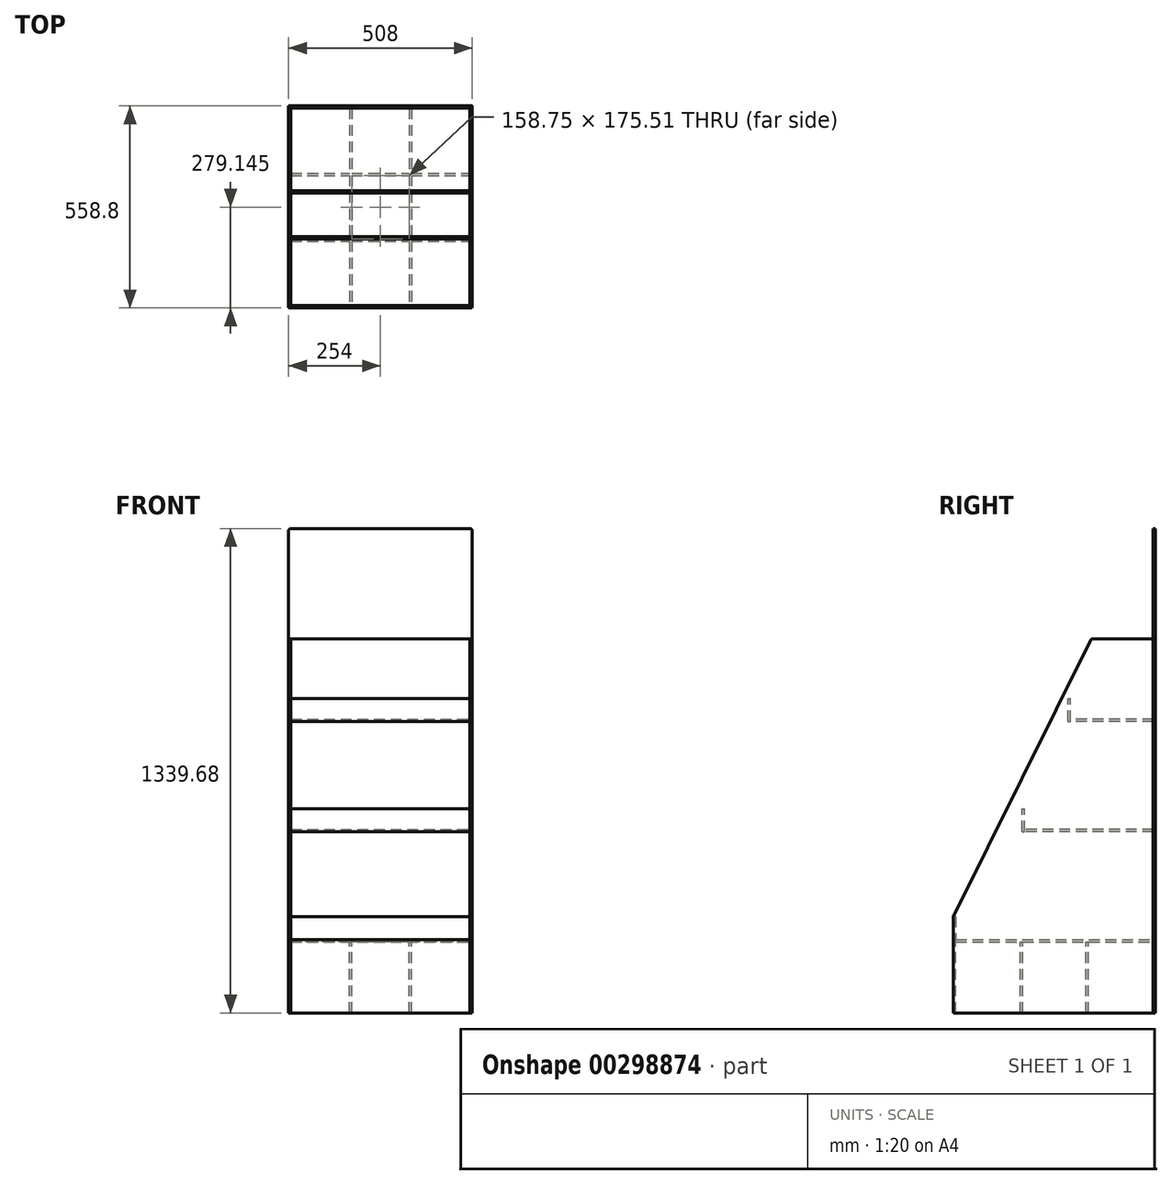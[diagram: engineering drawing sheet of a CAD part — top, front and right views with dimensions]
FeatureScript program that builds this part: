
annotation { "Feature Type Name" : "Feature", "Feature Type Description" : "" }
export const myFeature = defineFeature(function(context is Context, id is Id, definition is map)
    precondition{}
    {
        {
            var Q0;
            Q0=qCreatedBy(makeId("Right.planeOp"),FACE);
            var sketch = newSketch(context, id + "F0", { "sketchPlane" : qUnion([Q0])});
            skLineSegment(sketch, "E0", {"start": v(-313.65, -79.95) * mm, "end": v(245.15, -79.95) * mm});
            skLineSegment(sketch, "E1", {"start": v(245.15, 954.93) * mm, "end": v(67.35, 954.93) * mm});
            skLineSegment(sketch, "E2", {"start": v(-313.65, -79.95) * mm, "end": v(-313.65, 123.25) * mm});
            skLineSegment(sketch, "E3", {"start": v(-313.65, 123.25) * mm, "end": v(-313.65, 428.05) * mm, "construction": true});
            skLineSegment(sketch, "E4", {"start": v(-313.65, 428.05) * mm, "end": v(2.06, 428.05) * mm, "construction": true});
            skLineSegment(sketch, "E5", {"start": v(2.06, 428.05) * mm, "end": v(2.06, 732.85) * mm, "construction": true});
            skLineSegment(sketch, "E6", {"start": v(245.15, -79.95) * mm, "end": v(245.15, 954.93) * mm});
            skLineSegment(sketch, "E7", {"start": v(2.06, 732.85) * mm, "end": v(245.15, 732.85) * mm, "construction": true});
            skLineSegment(sketch, "E8", {"start": v(16.55, 732.85) * mm, "end": v(16.55, 796.35) * mm, "construction": true});
            skLineSegment(sketch, "E9", {"start": v(16.55, 796.35) * mm, "end": v(245.15, 796.35) * mm, "construction": true});
            skLineSegment(sketch, "E10", {"start": v(-313.65, 123.25) * mm, "end": v(-313.65, 186.75) * mm});
            skLineSegment(sketch, "E11", {"start": v(-313.65, 186.75) * mm, "end": v(67.35, 954.93) * mm});
            skSolve(sketch);
        }
        {
            var Q0;
            Q0 = qSketchRegion(id + "F0", true);
            extrude(context, id + "F1", {"entities" : qUnion([Q0]), "depth" : 6.35 * mm});
        }
        {
            var Q0;
            Q0=makeQuery(id+"F1.opExtrude","SWEPT_FACE",FACE,{"disambiguationData":[OSD([sQuery(id+"F0.wireOp",EDGE,"E6")])]});
            var sketch = newSketch(context, id + "F2", { "sketchPlane" : qUnion([Q0])});
            skLineSegment(sketch, "E12.bottom", {"start": v(-6.35, 954.93) * mm, "end": v(501.65, 954.93) * mm});
            skLineSegment(sketch, "E12.top", {"start": v(-6.35, -79.95) * mm, "end": v(501.65, -79.95) * mm});
            skLineSegment(sketch, "E12.left", {"start": v(-6.35, 954.93) * mm, "end": v(-6.35, -79.95) * mm});
            skLineSegment(sketch, "E12.right", {"start": v(501.65, 954.93) * mm, "end": v(501.65, -79.95) * mm});
            skSolve(sketch);
        }
        {
            var Q0;
            Q0 = qSketchRegion(id + "F2", true);
            extrude(context, id + "F3", {"entities" : qUnion([Q0]), "oppositeDirection" : true, "depth" : 6.35 * mm});
        }
        {
            var Q0;
            Q0=makeQuery(id+"F3.opExtrude","CAP_EDGE",EDGE,{"disambiguationData":[OSD([sQuery(id+"F2.wireOp",EDGE,"E12.bottom")])],"isStart":true});
            cPoint(context, id + "F4", {"entities" : qUnion([Q0]), "parameter" : 0.5});
        }
        {
            var Q0;
            Q0=qCreatedBy(makeId("Right.planeOp"),FACE);
            var Q1;
            Q1 = qCreatedBy(id + "F4" ,VERTEX);
            cPlane(context, id + "F5", {"entities" : qUnion([Q0, Q1]), "cplaneType" : CPlaneType.PLANE_POINT, "offset" : 25.4 * mm, "width" : 152.4 * mm, "height" : 152.4 * mm});
        }
        {
            var Q0;
            Q0=makeQuery(id+"F1.opExtrude","SWEPT_BODY",BODY,{"disambiguationData":[OSD([sQuery(id+"F0.wireOp",EDGE,"E0"),sQuery(id+"F0.wireOp",EDGE,"E1"),sQuery(id+"F0.wireOp",EDGE,"E2"),sQuery(id+"F0.wireOp",EDGE,"AbcFDwva-9bQH-yg0s-ynAT-r469iKRznc1V"),sQuery(id+"F0.wireOp",EDGE,"E6")])]});
            var Q1;
            Q1=qCreatedBy(id+"F5.planeOp",FACE);
            mirror(context, id + "F6", {"entities" : qUnion([Q0]), "mirrorPlane" : qUnion([Q1])});
        }
        {
            var Q0;
            Q0=makeQuery(id+"F6.opPattern","COPY",FACE,{"derivedFrom":makeQuery(id+"F1.opExtrude","SWEPT_FACE",FACE,{"disambiguationData":[OSD([sQuery(id+"F0.wireOp",EDGE,"E2")])]}),"instanceName":"1"});
            var sketch = newSketch(context, id + "F7", { "sketchPlane" : qUnion([Q0])});
            skLineSegment(sketch, "E13.bottom", {"start": v(-495.3, -79.95) * mm, "end": v(0, -79.95) * mm});
            skLineSegment(sketch, "E13.top", {"start": v(-495.3, 123.33) * mm, "end": v(0, 123.33) * mm});
            skLineSegment(sketch, "E13.left", {"start": v(-495.3, -79.95) * mm, "end": v(-495.3, 123.33) * mm});
            skLineSegment(sketch, "E13.right", {"start": v(0, -79.95) * mm, "end": v(0, 123.33) * mm});
            skSolve(sketch);
        }
        {
            var Q0;
            Q0 = qSketchRegion(id + "F7", true);
            extrude(context, id + "F8", {"entities" : qUnion([Q0]), "oppositeDirection" : true, "depth" : 6.35 * mm});
        }
        {
            var Q0;
            Q0=makeQuery(id+"F8.opExtrude","SWEPT_FACE",FACE,{"disambiguationData":[OSD([sQuery(id+"F7.wireOp",EDGE,"E13.top")])]});
            var sketch = newSketch(context, id + "F9", { "sketchPlane" : qUnion([Q0])});
            skLineSegment(sketch, "E14.bottom", {"start": v(-495.3, -313.65) * mm, "end": v(0, -313.65) * mm});
            skLineSegment(sketch, "E14.top", {"start": v(-495.3, 238.8) * mm, "end": v(0, 238.8) * mm});
            skLineSegment(sketch, "E14.left", {"start": v(-495.3, -313.65) * mm, "end": v(-495.3, 238.8) * mm});
            skLineSegment(sketch, "E14.right", {"start": v(0, -313.65) * mm, "end": v(0, 238.8) * mm});
            skSolve(sketch);
        }
        {
            var Q0;
            {var subQ0=sQuery(id+"F9.wireOp",EDGE,"E14.top");Q0=makeQuery(id+"F9.imprint","IMPRINT",FACE,{"disambiguationData":[TD([[makeQuery(id+"F9.imprint","IMPRINT",EDGE,{"derivedFrom":subQ0}),-1.0]])]});}
            extrude(context, id + "F10", {"entities" : qUnion([Q0]), "oppositeDirection" : true, "depth" : 6.35 * mm});
        }
        {
            var Q0;
            Q0=qCreatedBy(makeId("Top.planeOp"),FACE);
            var Q1;
            Q1=sQuery(id+"F0.wireOp",VERTEX,"E5.start");
            cPlane(context, id + "F11", {"entities" : qUnion([Q0, Q1]), "cplaneType" : CPlaneType.PLANE_POINT, "offset" : 25.4 * mm, "width" : 152.4 * mm, "height" : 152.4 * mm});
        }
        {
            var Q0;
            Q0=qCreatedBy(id+"F11.planeOp",FACE);
            var sketch = newSketch(context, id + "F12", { "sketchPlane" : qUnion([Q0])});
            skLineSegment(sketch, "E15.0", {"start": v(6.35, 238.8) * mm, "end": v(-501.65, 238.8) * mm, "construction": true});
            skLineSegment(sketch, "E16.bottom", {"start": v(-495.3, 238.8) * mm, "end": v(0, 238.8) * mm});
            skLineSegment(sketch, "E16.top", {"start": v(-495.3, -116.8) * mm, "end": v(0, -116.8) * mm});
            skLineSegment(sketch, "E16.left", {"start": v(-495.3, 238.8) * mm, "end": v(-495.3, -116.8) * mm});
            skLineSegment(sketch, "E16.right", {"start": v(0, 238.8) * mm, "end": v(0, -116.8) * mm});
            skSolve(sketch);
        }
        {
            var Q0;
            Q0 = qSketchRegion(id + "F12", true);
            extrude(context, id + "F13", {"entities" : qUnion([Q0]), "oppositeDirection" : true, "depth" : 6.35 * mm});
        }
        {
            var Q0;
            Q0=makeQuery(id+"F13.opExtrude","SWEPT_FACE",FACE,{"disambiguationData":[OSD([sQuery(id+"F12.wireOp",EDGE,"E16.top")])]});
            var sketch = newSketch(context, id + "F14", { "sketchPlane" : qUnion([Q0])});
            skLineSegment(sketch, "E17.0", {"start": v(-495.3, 421.7) * mm, "end": v(0, 421.7) * mm, "construction": true});
            skLineSegment(sketch, "E18.bottom", {"start": v(-495.3, 421.7) * mm, "end": v(0, 421.7) * mm});
            skLineSegment(sketch, "E18.top", {"start": v(-495.3, 485.2) * mm, "end": v(0, 485.2) * mm});
            skLineSegment(sketch, "E18.left", {"start": v(-495.3, 421.7) * mm, "end": v(-495.3, 485.2) * mm});
            skLineSegment(sketch, "E18.right", {"start": v(0, 421.7) * mm, "end": v(0, 485.2) * mm});
            skSolve(sketch);
        }
        {
            var Q0;
            Q0 = qSketchRegion(id + "F14", true);
            extrude(context, id + "F15", {"entities" : qUnion([Q0]), "depth" : 6.35 * mm});
        }
        {
            var Q0;
            Q0=qCreatedBy(makeId("Top.planeOp"),FACE);
            var Q1;
            Q1=sQuery(id+"F0.wireOp",VERTEX,"E8.start");
            cPlane(context, id + "F16", {"entities" : qUnion([Q0, Q1]), "cplaneType" : CPlaneType.PLANE_POINT, "offset" : 25.4 * mm, "width" : 152.4 * mm, "height" : 152.4 * mm});
        }
        {
            var Q0;
            Q0=qCreatedBy(id+"F16.planeOp",FACE);
            var sketch = newSketch(context, id + "F17", { "sketchPlane" : qUnion([Q0])});
            skLineSegment(sketch, "E19.0", {"start": v(6.35, 238.8) * mm, "end": v(-501.65, 238.8) * mm, "construction": true});
            skLineSegment(sketch, "E20.0", {"start": v(-495.3, 245.15) * mm, "end": v(-495.3, 245.15) * mm});
            skLineSegment(sketch, "E21.bottom", {"start": v(-495.3, 238.8) * mm, "end": v(0, 238.8) * mm});
            skLineSegment(sketch, "E21.top", {"start": v(-495.3, 10.2) * mm, "end": v(0, 10.2) * mm});
            skLineSegment(sketch, "E21.left", {"start": v(-495.3, 238.8) * mm, "end": v(-495.3, 10.2) * mm});
            skLineSegment(sketch, "E21.right", {"start": v(0, 238.8) * mm, "end": v(0, 10.2) * mm});
            skSolve(sketch);
        }
        {
            var Q0;
            Q0 = qSketchRegion(id + "F17", true);
            extrude(context, id + "F18", {"entities" : qUnion([Q0]), "oppositeDirection" : true, "depth" : 6.35 * mm});
        }
        {
            var Q0;
            Q0=makeQuery(id+"F18.opExtrude","SWEPT_FACE",FACE,{"disambiguationData":[OSD([sQuery(id+"F17.wireOp",EDGE,"E21.top")])]});
            var sketch = newSketch(context, id + "F19", { "sketchPlane" : qUnion([Q0])});
            skLineSegment(sketch, "E22.bottom", {"start": v(-495.3, 726.5) * mm, "end": v(0, 726.5) * mm});
            skLineSegment(sketch, "E22.top", {"start": v(-495.3, 790) * mm, "end": v(0, 790) * mm});
            skLineSegment(sketch, "E22.left", {"start": v(-495.3, 726.5) * mm, "end": v(-495.3, 790) * mm});
            skLineSegment(sketch, "E22.right", {"start": v(0, 726.5) * mm, "end": v(0, 790) * mm});
            skSolve(sketch);
        }
        {
            var Q0;
            Q0 = qSketchRegion(id + "F19", true);
            extrude(context, id + "F20", {"entities" : qUnion([Q0]), "depth" : 6.35 * mm});
        }
        {
            var Q0;
            Q0=makeQuery(id+"F3.opExtrude","SWEPT_FACE",FACE,{"disambiguationData":[OSD([sQuery(id+"F2.wireOp",EDGE,"E12.bottom")])]});
            var sketch = newSketch(context, id + "F21", { "sketchPlane" : qUnion([Q0])});
            skLineSegment(sketch, "E23.bottom", {"start": v(-501.65, 245.15) * mm, "end": v(6.35, 245.15) * mm});
            skLineSegment(sketch, "E23.top", {"start": v(-501.65, 238.8) * mm, "end": v(6.35, 238.8) * mm});
            skLineSegment(sketch, "E23.left", {"start": v(-501.65, 245.15) * mm, "end": v(-501.65, 238.8) * mm});
            skLineSegment(sketch, "E23.right", {"start": v(6.35, 245.15) * mm, "end": v(6.35, 238.8) * mm});
            skSolve(sketch);
        }
        {
            var Q0;
            Q0 = qSketchRegion(id + "F21", true);
            extrude(context, id + "F22", {"entities" : qUnion([Q0]), "depth" : 304.8 * mm});
        }
        {
            var Q0;
            Q0=makeQuery(id+"F22.opExtrude","CAP_EDGE",EDGE,{"disambiguationData":[OSD([sQuery(id+"F21.wireOp",EDGE,"E23.right")])],"isStart":false});
            var Q1;
            Q1=makeQuery(id+"F22.opExtrude","CAP_EDGE",EDGE,{"disambiguationData":[OSD([sQuery(id+"F21.wireOp",EDGE,"E23.left")])],"isStart":false});
            fillet(context, id + "F23", {"entities" : qUnion([Q0, Q1]), "radius" : 6.35 * mm, "tangentPropagation" : true, "allowEdgeOverflow" : false});
        }
        {
            var Q0;
            Q0=makeQuery(id+"F10.opExtrude","CAP_FACE",FACE,{"disambiguationData":[OSD([sQuery(id+"F7.wireOp",EDGE,"E13.top"),sQuery(id+"F9.wireOp",EDGE,"E14.top"),sQuery(id+"F9.wireOp",EDGE,"E14.left"),sQuery(id+"F9.wireOp",EDGE,"E14.right")])],"isStart":false});
            var sketch = newSketch(context, id + "F24", { "sketchPlane" : qUnion([Q0])});
            skLineSegment(sketch, "E24", {"start": v(0, 125.44) * mm, "end": v(-495.3, 125.44) * mm, "construction": true});
            skLineSegment(sketch, "E25", {"start": v(0, -56.43) * mm, "end": v(-495.3, -56.43) * mm, "construction": true});
            skLineSegment(sketch, "E26", {"start": v(-165.1, 307.3) * mm, "end": v(-165.1, -238.8) * mm, "construction": true});
            skLineSegment(sketch, "E27", {"start": v(-330.2, 307.3) * mm, "end": v(-330.2, -238.8) * mm, "construction": true});
            skLineSegment(sketch, "E28.0", {"start": v(0, 128.61) * mm, "end": v(-495.3, 128.61) * mm});
            skLineSegment(sketch, "E29.0", {"start": v(0, 122.26) * mm, "end": v(-495.3, 122.26) * mm});
            skLineSegment(sketch, "E30.0", {"start": v(0, -53.25) * mm, "end": v(-495.3, -53.25) * mm});
            skLineSegment(sketch, "E31.0", {"start": v(0, -59.6) * mm, "end": v(-495.3, -59.6) * mm});
            skLineSegment(sketch, "E32.0", {"start": v(-168.28, 307.3) * mm, "end": v(-168.28, -238.8) * mm});
            skLineSegment(sketch, "E33.0", {"start": v(-161.93, 307.3) * mm, "end": v(-161.92, -238.8) * mm});
            skLineSegment(sketch, "E34.0", {"start": v(-333.38, 307.3) * mm, "end": v(-333.38, -238.8) * mm});
            skLineSegment(sketch, "E35.0", {"start": v(-327.03, 307.3) * mm, "end": v(-327.03, -238.8) * mm});
            skLineSegment(sketch, "E36", {"start": v(-168.28, 307.3) * mm, "end": v(-161.93, 307.3) * mm});
            skLineSegment(sketch, "E37", {"start": v(0, 128.61) * mm, "end": v(0, 122.26) * mm});
            skLineSegment(sketch, "E38", {"start": v(0, -53.25) * mm, "end": v(0, -59.6) * mm});
            skLineSegment(sketch, "E39", {"start": v(-168.28, -238.8) * mm, "end": v(-161.92, -238.8) * mm});
            skLineSegment(sketch, "E40", {"start": v(-333.38, -238.8) * mm, "end": v(-327.03, -238.8) * mm});
            skLineSegment(sketch, "E41", {"start": v(-495.3, -53.25) * mm, "end": v(-495.3, -59.6) * mm});
            skLineSegment(sketch, "E42", {"start": v(-495.3, 128.61) * mm, "end": v(-495.3, 122.26) * mm});
            skLineSegment(sketch, "E43", {"start": v(-333.38, 307.3) * mm, "end": v(-327.03, 307.3) * mm});
            skSolve(sketch);
        }
        {
            var Q0;
            Q0 = qSketchRegion(id + "F24", true);
            var Q1;
            {var subQ0=sQuery(id+"F24.wireOp",EDGE,"E35.0");var subQ1=sQuery(id+"F24.wireOp",EDGE,"E28.0");var subQ2=makeQuery(id+"F24.imprint","INTERSECT",VERTEX,{"derivedFrom":[subQ1,subQ0]});Q1=makeQuery(id+"F24.imprint","IMPRINT",FACE,{"disambiguationData":[TD([[makeQuery(id+"F24.imprint","IMPRINT",EDGE,{"disambiguationData":[TD([[subQ2,-1.0]])],"derivedFrom":subQ1}),-1.0]])]});}
            var Q2;
            Q2=makeQuery(id+"F1.opExtrude","SWEPT_FACE",FACE,{"disambiguationData":[OSD([sQuery(id+"F0.wireOp",EDGE,"E0")])]});
            extrude(context, id + "F25", {"entities" : qUnion([Q0, Q1]), "endBound" : BoundingType.UP_TO_SURFACE, "endBoundEntityFace" : qUnion([Q2]), "depth" : 25.4 * mm});
        }
        {
            var Q0;
            Q0=makeQuery(id+"F8.opExtrude","SWEPT_FACE",FACE,{"disambiguationData":[OSD([sQuery(id+"F7.wireOp",EDGE,"E13.top")])]});
            var sketch = newSketch(context, id + "F26", { "sketchPlane" : qUnion([Q0])});
            skLineSegment(sketch, "E44.bottom", {"start": v(-495.3, -307.3) * mm, "end": v(0, -307.3) * mm});
            skLineSegment(sketch, "E44.top", {"start": v(-495.3, -313.65) * mm, "end": v(0, -313.65) * mm});
            skLineSegment(sketch, "E44.left", {"start": v(-495.3, -307.3) * mm, "end": v(-495.3, -313.65) * mm});
            skLineSegment(sketch, "E44.right", {"start": v(0, -307.3) * mm, "end": v(0, -313.65) * mm});
            skSolve(sketch);
        }
        {
            var Q0;
            Q0 = qSketchRegion(id + "F26", true);
            var Q1;
            Q1=makeQuery(id+"F6.opPattern","COPY",FACE,{"derivedFrom":makeQuery(id+"F1.opExtrude","SWEPT_FACE",FACE,{"disambiguationData":[OSD([sQuery(id+"F0.wireOp",EDGE,"7ldSreHR-QihD-k5D2-oDa8-QoOn2SvYhU5C")])]}),"instanceName":"1"});
            var Q2;
            Q2=makeQuery(id+"F6.opPattern","COPY",VERTEX,{"derivedFrom":makeQuery(id+"F1.opExtrude","CAP_VERTEX",VERTEX,{"disambiguationData":[OSD([sQuery(id+"F0.wireOp",EDGE,"E10"),sQuery(id+"F0.wireOp",EDGE,"E11")])],"isStart":true}),"instanceName":"1"});
            extrude(context, id + "F27", {"entities" : qUnion([Q0]), "endBound" : BoundingType.UP_TO_VERTEX, "endBoundEntityFace" : qUnion([Q1]), "endBoundEntityVertex" : qUnion([Q2]), "depth" : 25.4 * mm});
        }
        {
            var Q0;
            Q0=makeQuery(id+"F6.opPattern","COPY",EDGE,{"derivedFrom":makeQuery(id+"F1.opExtrude","SWEPT_EDGE",EDGE,{"disambiguationData":[OSD([sQuery(id+"F0.wireOp",EDGE,"E1"),sQuery(id+"F0.wireOp",EDGE,"E11")])]}),"instanceName":"1"});
            var Q1;
            Q1=makeQuery(id+"F1.opExtrude","SWEPT_EDGE",EDGE,{"disambiguationData":[OSD([sQuery(id+"F0.wireOp",EDGE,"E1"),sQuery(id+"F0.wireOp",EDGE,"E11")])]});
            fillet(context, id + "F28", {"entities" : qUnion([Q0, Q1]), "radius" : 6.35 * mm, "tangentPropagation" : true, "allowEdgeOverflow" : false});
        }
    });
